# Revit family: 1441xxx Edward Desk (CE and UL)
name_source: partatom
category: Lighting Fixtures
units: mm (PartAtom-declared; Revit-internal decimal feet)

## family parameters
Always vertical = Yes
Cut with Voids When Loaded = No
Light Source = No
OmniClass Number = 23.80.70.00
OmniClass Title = Lighting
Part Type = Normal
Room Calculation Point = No
Round Connector Dimension = Use Diameter
Shared = No
Work Plane-Based = No

## types (2) — shared parameters
Apparent Load = 0 VA
Dimmable = Remote dimmer required
Dimming Method = Lamp dependent
Efficacy (lm/W) = Lamp dependent
Electrical Class = 1
Light Source Fixed = no
Main Finish = Matt Black and Matt Gold
Main Material = Metal - Mild Steel / Zinc
Manufacturer URL - Europe and Rest of World = www.astrolighting.com
Manufacturer URL - North America = us.astrolighting.com
Power (W) = Lamp dependent
Product CCT = Lamp dependent
Product CRI = Lamp dependent
Product Location = Table / Desk
Product Name = Edward Desk
Wattage Comments = 12W Max
zero-valued in all types: Default Elevation

## per-type parameters (varying)
| type | ADA compliant | Lamp | Length of Cable Supplied | Location / IP Rating | Product Dimensions | Product SKU | Product URL | Product Weight |
| Astro Edward Desk ( UL ) | Yes - if installed in compliance with ADA §307.2, 308, 309.3, 309.4 | 1 x E26 | 78 Inch | Indoor / DRY | 21.4 x 7.7 x 14.3 Inch | 1441009 | https://us.astrolighting.com | 13.2 Lb |
| Astro Edward Desk ( CE ) |  | 1 x E27 | 2000 MM | Indoor / IP20 | 543 x 195 x 364 KG | 1441003 | https://www.astrolighting.com | 6 KG |

## geometry (parser evidence)
native form markers: Sweep x3
no freeform markers — native parametric forms only
